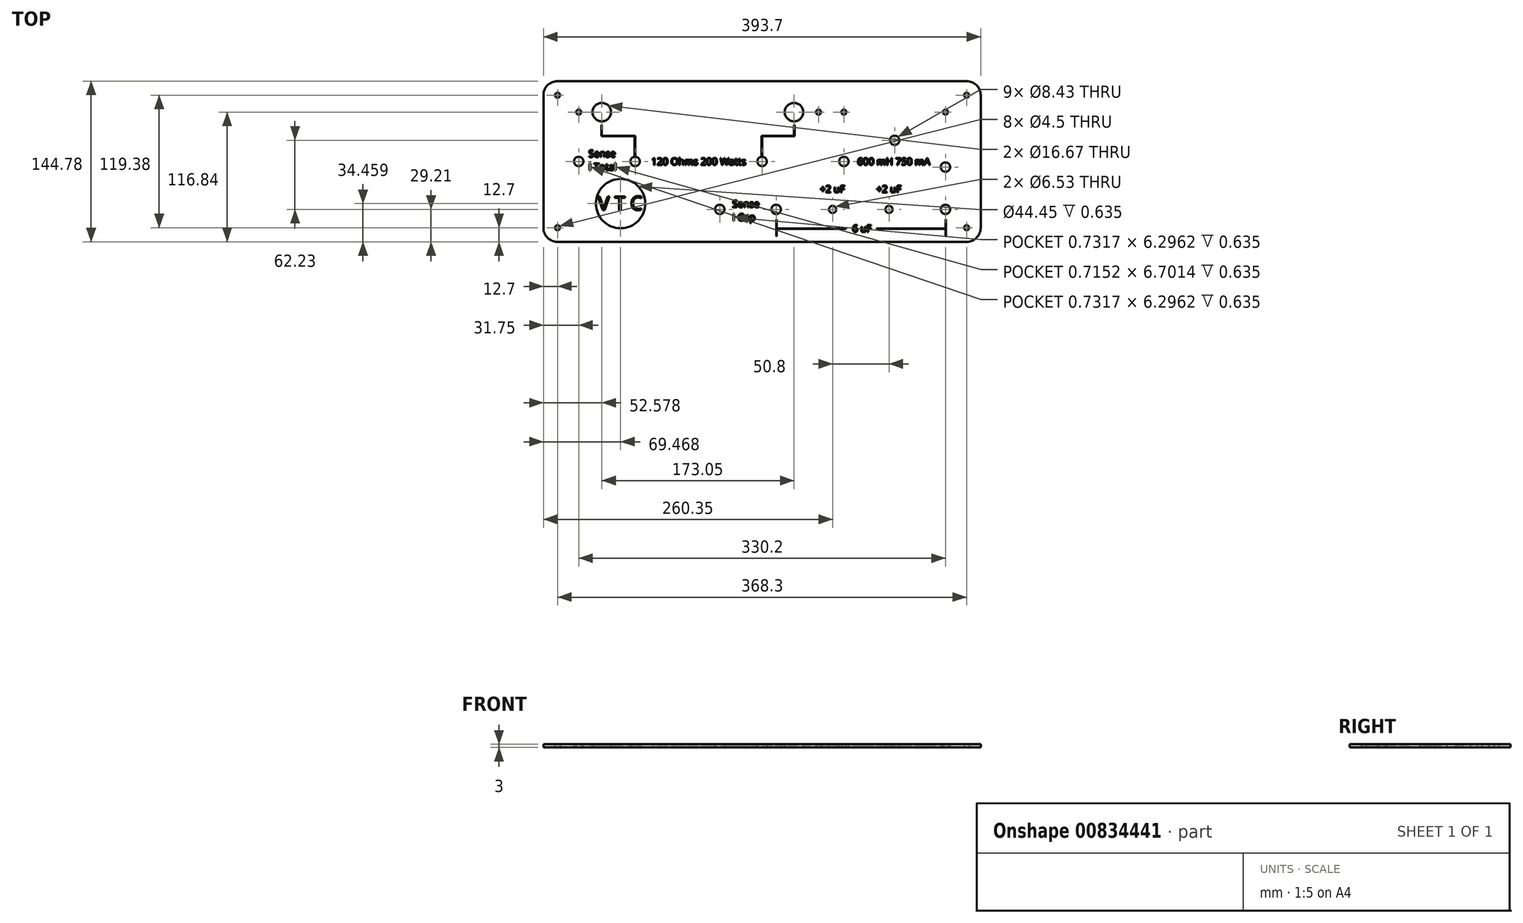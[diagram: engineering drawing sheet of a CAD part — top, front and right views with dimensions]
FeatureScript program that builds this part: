
annotation { "Feature Type Name" : "Feature", "Feature Type Description" : "" }
export const myFeature = defineFeature(function(context is Context, id is Id, definition is map)
    precondition{}
    {
        {
            var Q0;
            Q0=qCreatedBy(makeId("Top.planeOp"),FACE);
            var sketch = newSketch(context, id + "F0", { "sketchPlane" : qUnion([Q0])});
            skLineSegment(sketch, "E0.bottom", {"start": v(184.15, 72.4) * mm, "end": v(-184.15, 72.4) * mm});
            skLineSegment(sketch, "E0.top", {"start": v(184.15, -72.39) * mm, "end": v(-184.15, -72.39) * mm});
            skLineSegment(sketch, "E0.left", {"start": v(196.85, 59.7) * mm, "end": v(196.85, -59.69) * mm});
            skLineSegment(sketch, "E0.right", {"start": v(-196.85, 59.7) * mm, "end": v(-196.85, -59.69) * mm});
            skPoint(sketch, "E0.middle", {"position": v(0, 0) * mm});
            skPoint(sketch, "E1", {"position": v(-165.1, 44.45) * mm});
            skPoint(sketch, "E2", {"position": v(50.8, 44.45) * mm});
            skPoint(sketch, "E3", {"position": v(73.66, 44.45) * mm});
            skPoint(sketch, "E4", {"position": v(165.1, 44.45) * mm});
            skPoint(sketch, "E5", {"position": v(-144.27, 44.45) * mm});
            skPoint(sketch, "E6", {"position": v(28.78, 44.45) * mm});
            skPoint(sketch, "E7", {"position": v(-114.3, 0) * mm});
            skPoint(sketch, "E8", {"position": v(73.66, 0) * mm});
            skPoint(sketch, "E9", {"position": v(165.1, -5.08) * mm});
            skPoint(sketch, "E10", {"position": v(-165.1, 0) * mm});
            skPoint(sketch, "E11", {"position": v(-38.1, -43.18) * mm});
            skPoint(sketch, "E12", {"position": v(63.5, -43.18) * mm});
            skPoint(sketch, "E13", {"position": v(114.3, -43.18) * mm});
            skPoint(sketch, "E14", {"position": v(165.1, -43.18) * mm});
            skPoint(sketch, "E15", {"position": v(184.15, 59.7) * mm});
            skPoint(sketch, "E16", {"position": v(184.15, -59.69) * mm});
            skPoint(sketch, "E17", {"position": v(-184.15, -59.69) * mm});
            skPoint(sketch, "E18", {"position": v(-184.15, 59.7) * mm});
            skPoint(sketch, "E19", {"position": v(119.38, 19.05) * mm});
            skPoint(sketch, "E20.visualSharp", {"position": v(-196.85, 72.4) * mm});
            skArc(sketch, "E20.filletArc", {"start": v(-184.15, 72.4) * mm, "mid": v(-193.13, 68.67) * mm, "end": v(-196.85, 59.7) * mm});
            skPoint(sketch, "E21.visualSharp", {"position": v(196.85, 72.4) * mm});
            skArc(sketch, "E21.filletArc", {"start": v(196.85, 59.7) * mm, "mid": v(193.13, 68.67) * mm, "end": v(184.15, 72.4) * mm});
            skPoint(sketch, "E22.visualSharp", {"position": v(196.85, -72.39) * mm});
            skArc(sketch, "E22.filletArc", {"start": v(184.15, -72.39) * mm, "mid": v(193.13, -68.67) * mm, "end": v(196.85, -59.69) * mm});
            skPoint(sketch, "E23.visualSharp", {"position": v(-196.85, -72.39) * mm});
            skArc(sketch, "E23.filletArc", {"start": v(-196.85, -59.69) * mm, "mid": v(-193.13, -68.67) * mm, "end": v(-184.15, -72.39) * mm});
            skPoint(sketch, "E24", {"position": v(12.7, -43.18) * mm});
            skSolve(sketch);
        }
        {
            var Q0;
            Q0=qSketchRegion(id+"F0",true);
            extrude(context, id + "F1", {"entities" : qUnion([Q0]), "depth" : 3 * mm, "offsetDistance" : 25.4 * mm});
        }
        {
            var Q0;
            Q0=sQuery(id+"F0.wireOp",VERTEX,"E4");
            var Q1;
            Q1=sQuery(id+"F0.wireOp",VERTEX,"E3");
            var Q2;
            Q2=sQuery(id+"F0.wireOp",VERTEX,"E2");
            var Q3;
            Q3=sQuery(id+"F0.wireOp",VERTEX,"E1");
            var Q4;
            Q4=sQuery(id+"F0.wireOp",VERTEX,"E18");
            var Q5;
            Q5=sQuery(id+"F0.wireOp",VERTEX,"E17");
            var Q6;
            Q6=sQuery(id+"F0.wireOp",VERTEX,"E16");
            var Q7;
            Q7=sQuery(id+"F0.wireOp",VERTEX,"E15");
            var Q8;
            Q8=makeQuery(id+"F1.opExtrude","SWEPT_BODY",BODY,{"disambiguationData":[OSD([sQuery(id+"F0.wireOp",EDGE,"E0.bottom"),sQuery(id+"F0.wireOp",EDGE,"E0.top"),sQuery(id+"F0.wireOp",EDGE,"E0.left"),sQuery(id+"F0.wireOp",EDGE,"E0.right")])]});
            hole(context, id + "F2", {"style" : HoleStyle.SIMPLE, "endStyle" : HoleEndStyle.THROUGH, "oppositeDirection" : true, "standardTappedOrClearance" : lookupTablePath({ "standard" : "ANSI", "fit" : "Normal (ASME)", "size" : "#8", "type" : "Clearance" }), "standardBlindInLast" : lookupTablePath({ "fit" : "Free", "standard" : "ANSI", "size" : "#8", "type" : "Clearance" }), "holeDiameter" : 4.5 * mm, "majorDiameter" : 6.35 * mm, "isTappedThrough" : true, "tappedDepth" : 12.7 * mm, "tapClearance" : 3, "locations" : qUnion([Q0, Q1, Q2, Q3, Q4, Q5, Q6, Q7]), "scope" : qUnion([Q8])});
        }
        {
            var Q0;
            Q0=sQuery(id+"F0.wireOp",VERTEX,"E6");
            var Q1;
            Q1=sQuery(id+"F0.wireOp",VERTEX,"E5");
            var Q2;
            Q2=makeQuery(id+"F1.opExtrude","SWEPT_BODY",BODY,{"disambiguationData":[OSD([sQuery(id+"F0.wireOp",EDGE,"E0.bottom"),sQuery(id+"F0.wireOp",EDGE,"E0.top"),sQuery(id+"F0.wireOp",EDGE,"E0.left"),sQuery(id+"F0.wireOp",EDGE,"E0.right")])]});
            hole(context, id + "F3", {"style" : HoleStyle.SIMPLE, "endStyle" : HoleEndStyle.THROUGH, "oppositeDirection" : true, "standardTappedOrClearance" : lookupTablePath({ "standard" : "ANSI", "fit" : "Normal (ASME)", "size" : "5/8", "type" : "Clearance" }), "standardBlindInLast" : lookupTablePath({ "fit" : "Free", "standard" : "ANSI", "size" : "5/8", "type" : "Clearance" }), "holeDiameter" : 16.67 * mm, "majorDiameter" : 6.35 * mm, "isTappedThrough" : true, "tappedDepth" : 12.7 * mm, "tapClearance" : 3, "locations" : qUnion([Q0, Q1]), "scope" : qUnion([Q2])});
        }
        {
            var Q0;
            Q0=sQuery(id+"F0.wireOp",VERTEX,"E9");
            var Q1;
            Q1=sQuery(id+"F0.wireOp",VERTEX,"E8");
            var Q2;
            Q2=sQuery(id+"F0.wireOp",VERTEX,"E0.middle");
            var Q3;
            Q3=sQuery(id+"F0.wireOp",VERTEX,"E7");
            var Q4;
            Q4=sQuery(id+"F0.wireOp",VERTEX,"E14");
            var Q5;
            Q5=sQuery(id+"F0.wireOp",VERTEX,"E11");
            var Q6;
            Q6=sQuery(id+"F0.wireOp",VERTEX,"E10");
            var Q7;
            Q7=sQuery(id+"F0.wireOp",VERTEX,"E19");
            var Q8;
            Q8=sQuery(id+"F0.wireOp",VERTEX,"E24");
            var Q9;
            Q9=makeQuery(id+"F1.opExtrude","SWEPT_BODY",BODY,{"disambiguationData":[OSD([sQuery(id+"F0.wireOp",EDGE,"E0.bottom"),sQuery(id+"F0.wireOp",EDGE,"E0.top"),sQuery(id+"F0.wireOp",EDGE,"E0.left"),sQuery(id+"F0.wireOp",EDGE,"E0.right")])]});
            hole(context, id + "F4", {"style" : HoleStyle.SIMPLE, "endStyle" : HoleEndStyle.THROUGH, "oppositeDirection" : true, "standardTappedOrClearance" : lookupTablePath({ "standard" : "ANSI", "fit" : "Normal (ASME)", "size" : "5/16", "type" : "Clearance" }), "standardBlindInLast" : lookupTablePath({ "fit" : "Free", "standard" : "ANSI", "size" : "5/16", "type" : "Clearance" }), "holeDiameter" : 8.43 * mm, "majorDiameter" : 6.35 * mm, "isTappedThrough" : true, "tappedDepth" : 12.7 * mm, "tapClearance" : 3, "locations" : qUnion([Q0, Q1, Q2, Q3, Q4, Q5, Q6, Q7, Q8]), "scope" : qUnion([Q9])});
        }
        {
            var Q0;
            Q0=sQuery(id+"F0.wireOp",VERTEX,"E12");
            var Q1;
            Q1=sQuery(id+"F0.wireOp",VERTEX,"E13");
            var Q2;
            Q2=makeQuery(id+"F1.opExtrude","SWEPT_BODY",BODY,{"disambiguationData":[OSD([sQuery(id+"F0.wireOp",EDGE,"E0.bottom"),sQuery(id+"F0.wireOp",EDGE,"E0.top"),sQuery(id+"F0.wireOp",EDGE,"E0.left"),sQuery(id+"F0.wireOp",EDGE,"E0.right")])]});
            hole(context, id + "F5", {"style" : HoleStyle.SIMPLE, "endStyle" : HoleEndStyle.THROUGH, "oppositeDirection" : true, "standardTappedOrClearance" : lookupTablePath({ "standard" : "ANSI", "fit" : "Close", "size" : "1/4", "type" : "Clearance" }), "standardBlindInLast" : lookupTablePath({ "fit" : "Close", "standard" : "ANSI", "size" : "1/4", "type" : "Clearance" }), "holeDiameter" : 6.53 * mm, "majorDiameter" : 6.35 * mm, "isTappedThrough" : true, "tappedDepth" : 12.7 * mm, "tapClearance" : 3, "locations" : qUnion([Q0, Q1]), "scope" : qUnion([Q2])});
        }
        {
            var Q0;
            Q0=makeQuery(id+"F1.opExtrude","CAP_FACE",FACE,{"disambiguationData":[OSD([sQuery(id+"F0.wireOp",EDGE,"E0.bottom"),sQuery(id+"F0.wireOp",EDGE,"E0.top"),sQuery(id+"F0.wireOp",EDGE,"E0.left"),sQuery(id+"F0.wireOp",EDGE,"E0.right")])],"isStart":false});
            var sketch = newSketch(context, id + "F6", { "sketchPlane" : qUnion([Q0])});
            skText(sketch, "E25", { "text": "120 Ohms 200 Watts", "fontName": "OpenSans-Regular.ttf"});
            skText(sketch, "E26", { "text": "600 mH 750 mA\n", "fontName": "OpenSans-Regular.ttf"});
            skText(sketch, "E27", { "text": "Sense\nI Total", "fontName": "OpenSans-Regular.ttf"});
            skText(sketch, "E28", { "text": "Sense\nI Cap", "fontName": "OpenSans-Regular.ttf"});
            skText(sketch, "E29", { "text": "+2 uF", "fontName": "OpenSans-Regular.ttf"});
            skText(sketch, "E30", { "text": "6 uF", "fontName": "OpenSans-Regular.ttf"});
            skText(sketch, "E31", { "text": "V T C", "fontName": "OpenSans-Regular.ttf"});
            skText(sketch, "E32", { "text": "+2 uF", "fontName": "OpenSans-Regular.ttf"});
            skLineSegment(sketch, "E33.bottom", {"start": v(13.2, -60.34) * mm, "end": v(75.58, -60.34) * mm});
            skLineSegment(sketch, "E33.top", {"start": v(13.2, -60.84) * mm, "end": v(75.58, -60.84) * mm});
            skLineSegment(sketch, "E33.left", {"start": v(13.2, -60.34) * mm, "end": v(13.2, -60.84) * mm});
            skLineSegment(sketch, "E33.right", {"start": v(75.58, -60.34) * mm, "end": v(75.58, -60.84) * mm});
            skLineSegment(sketch, "E34.bottom", {"start": v(13.2, -67.3) * mm, "end": v(12.7, -67.3) * mm});
            skLineSegment(sketch, "E34.top", {"start": v(13.2, -52.07) * mm, "end": v(12.7, -52.07) * mm});
            skLineSegment(sketch, "E34.left", {"start": v(13.2, -67.3) * mm, "end": v(13.2, -52.07) * mm});
            skLineSegment(sketch, "E34.right", {"start": v(12.7, -67.3) * mm, "end": v(12.7, -52.07) * mm});
            skLineSegment(sketch, "E35.bottom", {"start": v(165.1, -52.07) * mm, "end": v(165.6, -52.07) * mm});
            skLineSegment(sketch, "E35.top", {"start": v(165.1, -67.3) * mm, "end": v(165.6, -67.3) * mm});
            skLineSegment(sketch, "E35.left", {"start": v(165.1, -52.07) * mm, "end": v(165.1, -67.3) * mm});
            skLineSegment(sketch, "E35.right", {"start": v(165.6, -52.07) * mm, "end": v(165.6, -67.3) * mm});
            skLineSegment(sketch, "E36.bottom", {"start": v(102.87, -60.34) * mm, "end": v(165.1, -60.34) * mm});
            skLineSegment(sketch, "E36.top", {"start": v(102.87, -60.84) * mm, "end": v(165.1, -60.84) * mm});
            skLineSegment(sketch, "E36.left", {"start": v(102.87, -60.34) * mm, "end": v(102.87, -60.84) * mm});
            skLineSegment(sketch, "E36.right", {"start": v(165.1, -60.34) * mm, "end": v(165.1, -60.84) * mm});
            skCircle(sketch, "E37", {"center": v(-127.38, -37.93) * mm, "radius": 22.23 * mm});
            skPoint(sketch, "E38", {"position": v(81.26, -60.34) * mm});
            skLineSegment(sketch, "E39.bottom", {"start": v(-144.27, 22.63) * mm, "end": v(-114.3, 22.63) * mm});
            skLineSegment(sketch, "E39.top", {"start": v(-144.27, 23.14) * mm, "end": v(-114.3, 23.14) * mm});
            skLineSegment(sketch, "E39.left", {"start": v(-144.27, 22.63) * mm, "end": v(-144.27, 23.14) * mm});
            skLineSegment(sketch, "E39.right", {"start": v(-114.3, 22.63) * mm, "end": v(-114.3, 23.14) * mm});
            skLineSegment(sketch, "E40.bottom", {"start": v(-0.5, 22.63) * mm, "end": v(0, 22.63) * mm});
            skLineSegment(sketch, "E40.top", {"start": v(-0.5, 4.85) * mm, "end": v(0, 4.85) * mm});
            skLineSegment(sketch, "E40.left", {"start": v(-0.5, 22.63) * mm, "end": v(-0.5, 4.85) * mm});
            skLineSegment(sketch, "E40.right", {"start": v(0, 22.63) * mm, "end": v(0, 4.85) * mm});
            skLineSegment(sketch, "E41.bottom", {"start": v(-114.3, 22.63) * mm, "end": v(-114.8, 22.63) * mm});
            skLineSegment(sketch, "E41.top", {"start": v(-114.3, 4.85) * mm, "end": v(-114.8, 4.85) * mm});
            skLineSegment(sketch, "E41.left", {"start": v(-114.3, 22.63) * mm, "end": v(-114.3, 4.85) * mm});
            skLineSegment(sketch, "E41.right", {"start": v(-114.8, 22.63) * mm, "end": v(-114.8, 4.85) * mm});
            skLineSegment(sketch, "E42.bottom", {"start": v(-144.27, 22.63) * mm, "end": v(-144.78, 22.63) * mm});
            skLineSegment(sketch, "E42.top", {"start": v(-144.27, 32.8) * mm, "end": v(-144.78, 32.8) * mm});
            skLineSegment(sketch, "E42.left", {"start": v(-144.27, 22.63) * mm, "end": v(-144.27, 32.8) * mm});
            skLineSegment(sketch, "E42.right", {"start": v(-144.78, 22.63) * mm, "end": v(-144.78, 32.8) * mm});
            skLineSegment(sketch, "E43.bottom", {"start": v(-0.5, 22.63) * mm, "end": v(28.78, 22.63) * mm});
            skLineSegment(sketch, "E43.top", {"start": v(-0.5, 23.14) * mm, "end": v(28.78, 23.14) * mm});
            skLineSegment(sketch, "E43.left", {"start": v(-0.5, 22.63) * mm, "end": v(-0.5, 23.14) * mm});
            skLineSegment(sketch, "E43.right", {"start": v(28.78, 22.63) * mm, "end": v(28.78, 23.14) * mm});
            skLineSegment(sketch, "E44.bottom", {"start": v(28.78, 22.63) * mm, "end": v(29.29, 22.63) * mm});
            skLineSegment(sketch, "E44.top", {"start": v(28.78, 32.8) * mm, "end": v(29.29, 32.8) * mm});
            skLineSegment(sketch, "E44.left", {"start": v(28.78, 22.63) * mm, "end": v(28.78, 32.8) * mm});
            skLineSegment(sketch, "E44.right", {"start": v(29.29, 22.63) * mm, "end": v(29.29, 32.8) * mm});
            const initialGuessF6  = {"E25": [-0.0997, -0.00315, 1, 0, 0.00635], "E26": [0.08578, -0.00315, 1, 0, 0.00635], "E27": [-0.15617, 0.0039, 1, 0, 0.00635], "E28": [-0.02674, -0.04142, 1, 0, 0.00635], "E29": [0.10293, -0.02794, 1, 0, 0.00635], "E30": [0.08126, -0.06351, 1, 0, 0.00635], "E31": [-0.1477, -0.0438, 1, 0, 0.01254], "E32": [0.05213, -0.02794, 1, 0, 0.00635]};
            skSetInitialGuess(sketch, initialGuessF6);
            skSolve(sketch);
        }
        {
            var Q0;
            Q0=qSketchRegion(id+"F6",true);
            var Q1;
            Q1=sQuery(id+"F6.wireOp",EDGE,"oCKS1ljm-eama-LIJx-cTZt-sQQLRqpoYSN7");
            extrude(context, id + "F7", {"entities" : qUnion([Q0]), "operationType" : NewBodyOperationType.REMOVE, "surfaceEntities" : qUnion([Q1]), "oppositeDirection" : true, "depth" : 0.64 * mm, "offsetDistance" : 25.4 * mm});
        }
    });
